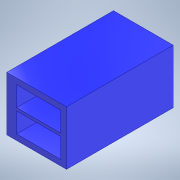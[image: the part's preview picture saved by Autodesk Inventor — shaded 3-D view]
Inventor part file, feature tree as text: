
AUTODESK INVENTOR PART (.ipt)
format: ipt  version: 2022 (Build 260153000, 153)  size: 141,312 bytes
history: native  units: mm
features: extrude x2, sketch x2, plane x1
ambient origin geometry x8: Origin, YZ Plane, XZ Plane, XY Plane, X Axis, Y Axis, Z Axis, Center Point
bodies: Solid1 (feature_tree)
feature tree (5):
  extrude  "Extrusion1"  Depth=14.0mm
  plane  "Work Plane5"
  extrude  "Extrusion4"  Depth=75.0mm TaperAngle=0.0deg
  sketch  "Sketch1"  dims[d1=31.0mm d2=12.0mm d3=14.0mm]
  sketch  "Sketch4"  dims[d4=14.0mm d5=75.0mm d6=0.0mm d7=4.0mm d25=2.0mm d26=7.0mm d27=4.0mm d28=32.004mm d29=32.004mm d30=5.08mm d31=0.0mm d32=19.0mm d33=19.0mm d34=-0.8mm]
